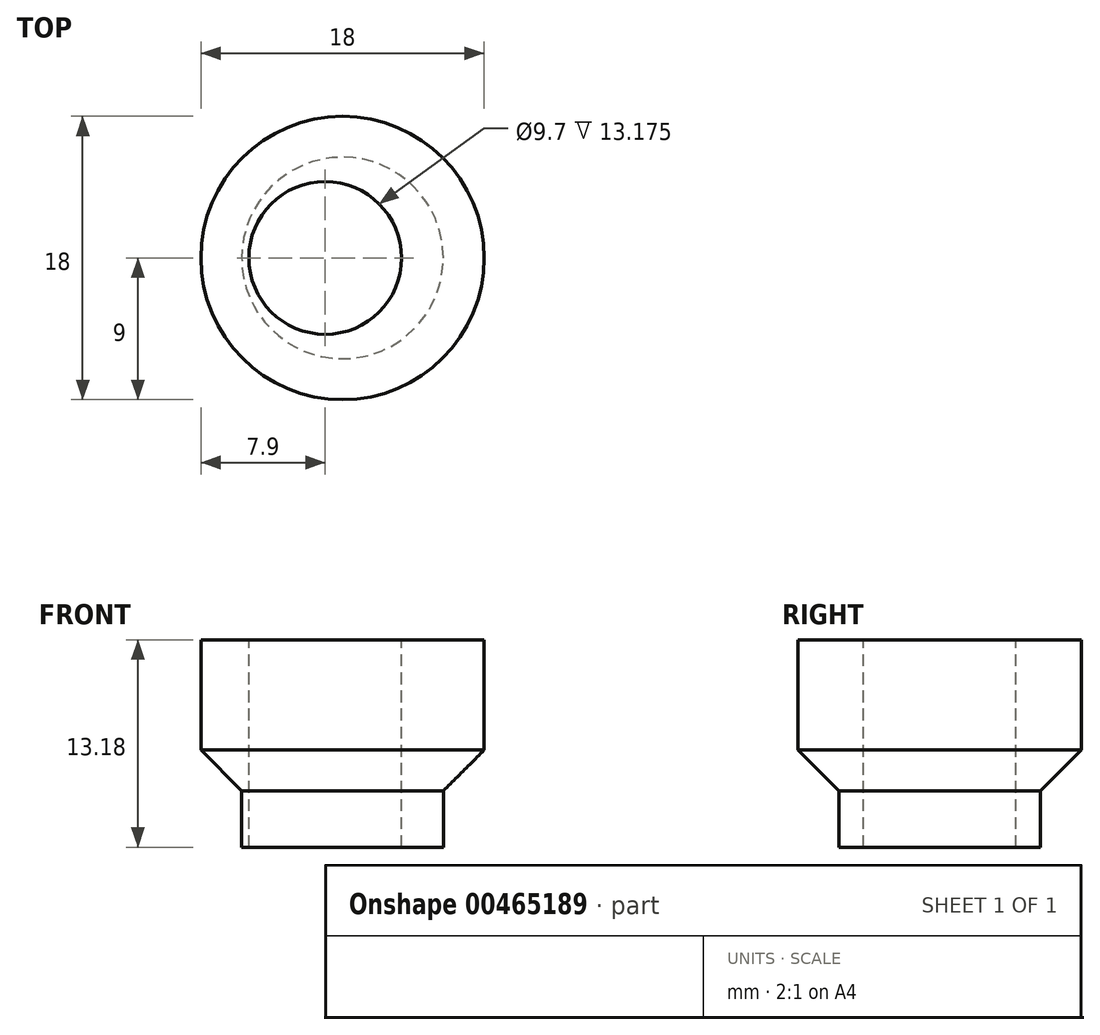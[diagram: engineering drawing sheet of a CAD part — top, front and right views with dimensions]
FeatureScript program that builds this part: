
annotation { "Feature Type Name" : "Feature", "Feature Type Description" : "" }
export const myFeature = defineFeature(function(context is Context, id is Id, definition is map)
    precondition{}
    {
        {
            var Q0;
            Q0=qCreatedBy(makeId("Front.planeOp"),FACE);
            var sketch = newSketch(context, id + "F0", { "sketchPlane" : qUnion([Q0])});
            skLineSegment(sketch, "E0.bottom", {"start": v(6.4, 1.59) * mm, "end": v(-6.4, 1.59) * mm});
            skLineSegment(sketch, "E0.top", {"start": v(6.4, -1.59) * mm, "end": v(-6.4, -1.59) * mm});
            skLineSegment(sketch, "E0.left", {"start": v(6.4, 1.59) * mm, "end": v(6.4, -1.59) * mm});
            skLineSegment(sketch, "E0.right", {"start": v(-6.4, 1.59) * mm, "end": v(-6.4, -1.59) * mm});
            skPoint(sketch, "E0.middle", {"position": v(0, 0) * mm});
            skLineSegment(sketch, "E1.bottom", {"start": v(9, 1.59) * mm, "end": v(-9, 1.59) * mm});
            skLineSegment(sketch, "E1.top", {"start": v(9, 11.59) * mm, "end": v(-9, 11.59) * mm});
            skLineSegment(sketch, "E1.left", {"start": v(9, 1.59) * mm, "end": v(9, 11.59) * mm});
            skLineSegment(sketch, "E1.right", {"start": v(-9, 1.59) * mm, "end": v(-9, 11.59) * mm});
            skLineSegment(sketch, "E2", {"start": v(0, 11.59) * mm, "end": v(0, 1.59) * mm});
            skLineSegment(sketch, "E3", {"start": v(0, 1.59) * mm, "end": v(0, -1.59) * mm});
            skSolve(sketch);
        }
        {
            var Q0;
            {var subQ0=sQuery(id+"F0.wireOp",EDGE,"E0.left");Q0=makeQuery(id+"F0.imprint","IMPRINT",FACE,{"disambiguationData":[TD([[makeQuery(id+"F0.imprint","IMPRINT",EDGE,{"derivedFrom":subQ0}),-1.0]])]});}
            var Q1;
            {var subQ0=sQuery(id+"F0.wireOp",EDGE,"E1.left");Q1=makeQuery(id+"F0.imprint","IMPRINT",FACE,{"disambiguationData":[TD([[makeQuery(id+"F0.imprint","IMPRINT",EDGE,{"derivedFrom":subQ0}),1.0]])]});}
            var Q2;
            Q2=sQuery(id+"F0.wireOp",EDGE,"E2");
            revolve(context, id + "F1", {"entities" : qUnion([Q0, Q1]), "axis" : qUnion([Q2]), "revolveType" : RevolveType.FULL});
        }
        {
            var Q0;
            Q0=makeQuery(id+"F1.opRevolve","SWEPT_EDGE",EDGE,{"disambiguationData":[OSD([sQuery(id+"F0.wireOp",EDGE,"E1.bottom"),sQuery(id+"F0.wireOp",EDGE,"E1.left")])]});
            chamfer(context, id + "F2", {"entities" : qUnion([Q0]), "width" : 3 * mm, "tangentPropagation" : true});
        }
        {
            var Q0;
            Q0=qCreatedBy(makeId("Top.planeOp"),FACE);
            var sketch = newSketch(context, id + "F3", { "sketchPlane" : qUnion([Q0])});
            skCircle(sketch, "E4", {"center": v(-1.1, 0) * mm, "radius": 4.85 * mm});
            skLineSegment(sketch, "E5", {"start": v(-1.1, 0) * mm, "end": v(0, 0) * mm});
            skSolve(sketch);
        }
        {
            var Q0;
            Q0 = qSketchRegion(id + "F3", true);
            extrude(context, id + "F4", {"entities" : qUnion([Q0]), "operationType" : NewBodyOperationType.REMOVE, "oppositeDirection" : true, "depth" : 25 * mm, "hasSecondDirection" : true, "secondDirectionOppositeDirection" : false, "secondDirectionDepth" : 25 * mm});
        }
    });
